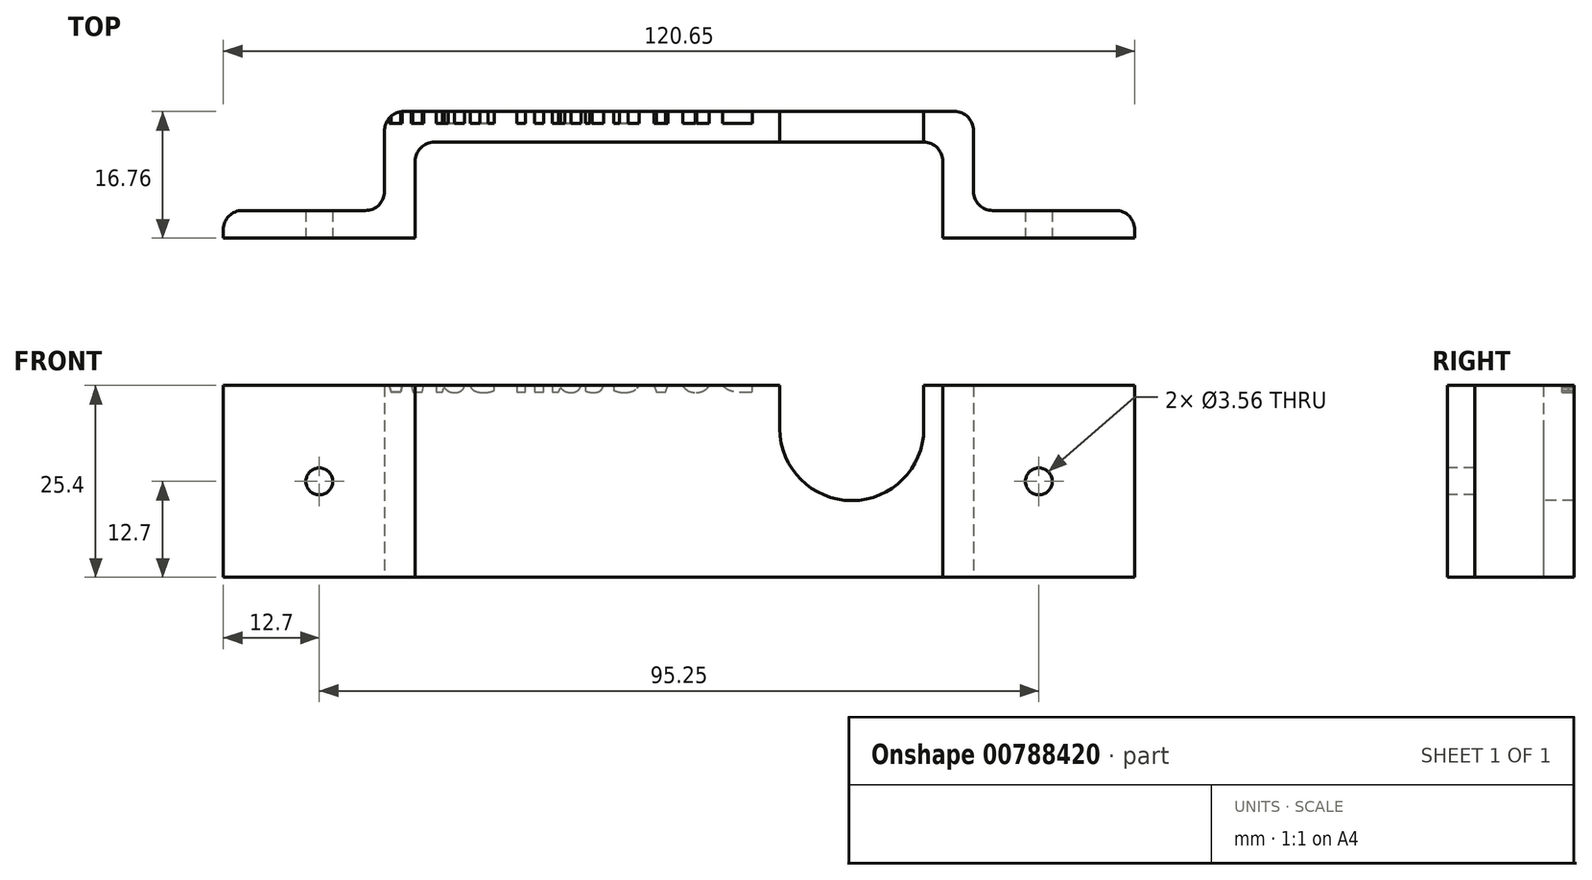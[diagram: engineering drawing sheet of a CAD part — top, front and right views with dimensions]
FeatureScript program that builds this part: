
annotation { "Feature Type Name" : "Feature", "Feature Type Description" : "" }
export const myFeature = defineFeature(function(context is Context, id is Id, definition is map)
    precondition{}
    {
        {
            var Q0;
            Q0=qCreatedBy(makeId("Top.planeOp"),FACE);
            var sketch = newSketch(context, id + "F0", { "sketchPlane" : qUnion([Q0])});
            skLineSegment(sketch, "E0.bottom", {"start": v(-59.36, 3.65) * mm, "end": v(-43.1, 3.65) * mm});
            skLineSegment(sketch, "E0.top", {"start": v(-61.9, 0) * mm, "end": v(-43.02, 0) * mm});
            skLineSegment(sketch, "E0.left", {"start": v(-61.9, 1.11) * mm, "end": v(-61.9, 0) * mm});
            skLineSegment(sketch, "E0.right", {"start": v(-43.02, 4.57) * mm, "end": v(-43.02, 0) * mm});
            skLineSegment(sketch, "E1.bottom", {"start": v(39.95, 3.65) * mm, "end": v(56.2, 3.65) * mm});
            skLineSegment(sketch, "E1.top", {"start": v(39.87, 0) * mm, "end": v(58.75, 0) * mm});
            skLineSegment(sketch, "E1.left", {"start": v(39.87, 4.57) * mm, "end": v(39.87, 0) * mm});
            skLineSegment(sketch, "E1.right", {"start": v(58.75, 1.11) * mm, "end": v(58.75, 0) * mm});
            skLineSegment(sketch, "E2.bottom", {"start": v(-43.02, 0) * mm, "end": v(-36.5, 0) * mm});
            skLineSegment(sketch, "E2.top", {"start": v(-38.02, 16.76) * mm, "end": v(34.87, 16.76) * mm});
            skLineSegment(sketch, "E2.left", {"start": v(-40.56, 6.2) * mm, "end": v(-40.56, 14.22) * mm});
            skLineSegment(sketch, "E2.right", {"start": v(37.41, 6.2) * mm, "end": v(37.41, 14.22) * mm});
            skLineSegment(sketch, "E3.0", {"start": v(33.35, 0) * mm, "end": v(33.35, 10.16) * mm});
            skLineSegment(sketch, "E3.1", {"start": v(-33.96, 12.7) * mm, "end": v(30.8, 12.7) * mm});
            skLineSegment(sketch, "E3.2", {"start": v(-36.5, 0) * mm, "end": v(-36.5, 10.16) * mm});
            skLineSegment(sketch, "E4.trimOffspring", {"start": v(33.35, 0) * mm, "end": v(39.87, 0) * mm});
            skPoint(sketch, "E5.visualSharp", {"position": v(37.41, 16.76) * mm});
            skArc(sketch, "E5.filletArc", {"start": v(37.41, 14.22) * mm, "mid": v(36.67, 16.02) * mm, "end": v(34.87, 16.76) * mm});
            skPoint(sketch, "E6.visualSharp", {"position": v(-40.56, 16.76) * mm});
            skArc(sketch, "E6.filletArc", {"start": v(-38.02, 16.76) * mm, "mid": v(-39.82, 16.02) * mm, "end": v(-40.56, 14.22) * mm});
            skArc(sketch, "E7.filletArc", {"start": v(-43.1, 3.65) * mm, "mid": v(-41.3, 4.4) * mm, "end": v(-40.56, 6.2) * mm});
            skPoint(sketch, "E8.visualSharp", {"position": v(33.35, 12.7) * mm});
            skArc(sketch, "E8.filletArc", {"start": v(33.35, 10.16) * mm, "mid": v(32.6, 11.96) * mm, "end": v(30.8, 12.7) * mm});
            skPoint(sketch, "E9.visualSharp", {"position": v(-36.5, 12.7) * mm});
            skArc(sketch, "E9.filletArc", {"start": v(-33.96, 12.7) * mm, "mid": v(-35.76, 11.96) * mm, "end": v(-36.5, 10.16) * mm});
            skArc(sketch, "E10.filletArc", {"start": v(37.41, 6.2) * mm, "mid": v(38.16, 4.4) * mm, "end": v(39.95, 3.65) * mm});
            skPoint(sketch, "E11.visualSharp", {"position": v(58.75, 3.65) * mm});
            skArc(sketch, "E11.filletArc", {"start": v(58.75, 1.11) * mm, "mid": v(58, 2.9) * mm, "end": v(56.2, 3.65) * mm});
            skPoint(sketch, "E12.visualSharp", {"position": v(-61.9, 3.65) * mm});
            skArc(sketch, "E12.filletArc", {"start": v(-59.36, 3.65) * mm, "mid": v(-61.16, 2.9) * mm, "end": v(-61.9, 1.11) * mm});
            skSolve(sketch);
        }
        {
            var Q0;
            Q0=makeQuery(id+"F0.imprint","IMPRINT",FACE,{"disambiguationData":[TD([[makeQuery(id+"F0.imprint","IMPRINT",EDGE,{"derivedFrom":sQuery(id+"F0.wireOp",EDGE,"E0.bottom")}),-1.0]])]});
            var Q1;
            {var subQ4=sQuery(id+"F0.wireOp",EDGE,"E1.bottom");Q1=makeQuery(id+"F0.imprint","IMPRINT",FACE,{"disambiguationData":[TD([[makeQuery(id+"F0.imprint","IMPRINT",EDGE,{"derivedFrom":subQ4}),-1.0]])]});}
            var Q2;
            {var subQ3=sQuery(id+"F0.wireOp",EDGE,"E2.bottom");Q2=makeQuery(id+"F0.imprint","IMPRINT",FACE,{"disambiguationData":[TD([[makeQuery(id+"F0.imprint","IMPRINT",EDGE,{"derivedFrom":subQ3}),1.0]])]});}
            extrude(context, id + "F1", {"entities" : qUnion([Q0, Q1, Q2]), "depth" : 25.4 * mm, "offsetDistance" : 25.4 * mm});
        }
        {
            var Q0;
            Q0=makeQuery(id+"F1.opExtrude","SWEPT_FACE",FACE,{"disambiguationData":[OSD([sQuery(id+"F0.wireOp",EDGE,"E0.top"),sQuery(id+"F0.wireOp",EDGE,"E2.bottom")])]});
            var sketch = newSketch(context, id + "F2", { "sketchPlane" : qUnion([Q0])});
            skPoint(sketch, "E13", {"position": v(-49.2, 25.4) * mm});
            skPoint(sketch, "E14", {"position": v(-36.5, 12.7) * mm});
            skPoint(sketch, "E15", {"position": v(-61.9, 12.7) * mm});
            skPoint(sketch, "E16", {"position": v(-49.2, 0) * mm});
            skLineSegment(sketch, "E17", {"start": v(-61.9, 12.7) * mm, "end": v(-36.5, 12.7) * mm});
            skPoint(sketch, "E18", {"position": v(-49.2, 12.7) * mm});
            skLineSegment(sketch, "E19", {"start": v(-36.5, 12.7) * mm, "end": v(58.75, 12.7) * mm});
            skLineSegment(sketch, "E20", {"start": v(58.75, 12.7) * mm, "end": v(46.05, 12.7) * mm});
            skLineSegment(sketch, "E21", {"start": v(-61.9, 12.7) * mm, "end": v(-49.2, 12.7) * mm});
            skSolve(sketch);
        }
        {
            var Q0;
            Q0=sQuery(id+"F2.wireOp",VERTEX,"E18");
            var Q1;
            Q1=sQuery(id+"F2.wireOp",VERTEX,"E20.end");
            var Q2;
            Q2=makeQuery(id+"F1.opExtrude","SWEPT_BODY",BODY,{"disambiguationData":[OSD([sQuery(id+"F0.wireOp",EDGE,"E0.bottom"),sQuery(id+"F0.wireOp",EDGE,"E0.top"),sQuery(id+"F0.wireOp",EDGE,"E0.left"),sQuery(id+"F0.wireOp",EDGE,"E1.bottom"),sQuery(id+"F0.wireOp",EDGE,"E1.top"),sQuery(id+"F0.wireOp",EDGE,"E1.right"),sQuery(id+"F0.wireOp",EDGE,"E2.bottom"),sQuery(id+"F0.wireOp",EDGE,"E2.top"),sQuery(id+"F0.wireOp",EDGE,"E2.left"),sQuery(id+"F0.wireOp",EDGE,"E2.right"),sQuery(id+"F0.wireOp",EDGE,"E3.0"),sQuery(id+"F0.wireOp",EDGE,"E3.1"),sQuery(id+"F0.wireOp",EDGE,"E3.2"),sQuery(id+"F0.wireOp",EDGE,"E4.trimOffspring"),sQuery(id+"F0.wireOp",EDGE,"E5.filletArc"),sQuery(id+"F0.wireOp",EDGE,"E6.filletArc"),sQuery(id+"F0.wireOp",EDGE,"E7.filletArc"),sQuery(id+"F0.wireOp",EDGE,"E8.filletArc"),sQuery(id+"F0.wireOp",EDGE,"E9.filletArc"),sQuery(id+"F0.wireOp",EDGE,"E10.filletArc"),sQuery(id+"F0.wireOp",EDGE,"E11.filletArc"),sQuery(id+"F0.wireOp",EDGE,"E12.filletArc")])]});
            hole(context, id + "F3", {"style" : HoleStyle.C_SINK, "endStyle" : HoleEndStyle.THROUGH, "holeDiameter" : 3.56 * mm, "cSinkDiameter" : 3.56 * mm, "cSinkAngle" : 90 * degree, "majorDiameter" : 6.35 * mm, "isTappedThrough" : true, "tappedDepth" : 12.7 * mm, "tapClearance" : 3, "locations" : qUnion([Q0, Q1]), "scope" : qUnion([Q2])});
        }
        {
            var Q0;
            Q0=makeQuery(id+"F1.opExtrude","SWEPT_FACE",FACE,{"disambiguationData":[OSD([sQuery(id+"F0.wireOp",EDGE,"E3.1")])]});
            var sketch = newSketch(context, id + "F4", { "sketchPlane" : qUnion([Q0])});
            skLineSegment(sketch, "E22.bottom", {"start": v(30.8, 25.4) * mm, "end": v(11.76, 25.4) * mm});
            skLineSegment(sketch, "E22.top", {"start": v(21.28, 10.16) * mm, "end": v(21.28, 10.16) * mm});
            skLineSegment(sketch, "E22.left", {"start": v(30.8, 25.4) * mm, "end": v(30.8, 19.69) * mm});
            skLineSegment(sketch, "E22.right", {"start": v(11.76, 25.4) * mm, "end": v(11.76, 19.68) * mm});
            skPoint(sketch, "E23.visualSharp", {"position": v(11.76, 10.16) * mm});
            skArc(sketch, "E23.filletArc", {"start": v(11.76, 19.68) * mm, "mid": v(14.55, 12.95) * mm, "end": v(21.28, 10.16) * mm});
            skPoint(sketch, "E24.visualSharp", {"position": v(30.8, 10.16) * mm});
            skArc(sketch, "E24.filletArc", {"start": v(21.28, 10.16) * mm, "mid": v(28.02, 12.95) * mm, "end": v(30.8, 19.69) * mm});
            skSolve(sketch);
        }
        {
            var Q0;
            Q0=makeQuery(id+"F4.imprint","IMPRINT",FACE,{"disambiguationData":[TD([[makeQuery(id+"F4.imprint","IMPRINT",EDGE,{"derivedFrom":sQuery(id+"F4.wireOp",EDGE,"E22.bottom")}),-1.0]])]});
            extrude(context, id + "F5", {"entities" : qUnion([Q0]), "operationType" : NewBodyOperationType.REMOVE, "endBound" : BoundingType.THROUGH_ALL, "oppositeDirection" : true, "depth" : 25.4 * mm, "offsetDistance" : 25.4 * mm});
        }
        {
            var Q0;
            Q0=makeQuery(id+"F1.opExtrude","SWEPT_FACE",FACE,{"disambiguationData":[OSD([sQuery(id+"F0.wireOp",EDGE,"E2.top")])]});
            var sketch = newSketch(context, id + "F6", { "sketchPlane" : qUnion([Q0])});
            skText(sketch, "E25", { "text": "Dovetail saw\n", "fontName": "OpenSans-Bold.ttf"});
            skPoint(sketch, "E26", {"position": v(-11.76, 22.54) * mm});
            const initialGuessF6  = {"E25": [-0.00885, 0.02454, 1, 0, 0.00562]};
            skSetInitialGuess(sketch, initialGuessF6);
            skSolve(sketch);
        }
        {
            var Q0;
            Q0 = qSketchRegion(id + "F6", true);
            extrude(context, id + "F7", {"entities" : qUnion([Q0]), "operationType" : NewBodyOperationType.REMOVE, "oppositeDirection" : true, "depth" : 1.59 * mm, "offsetDistance" : 25.4 * mm});
        }
    });
